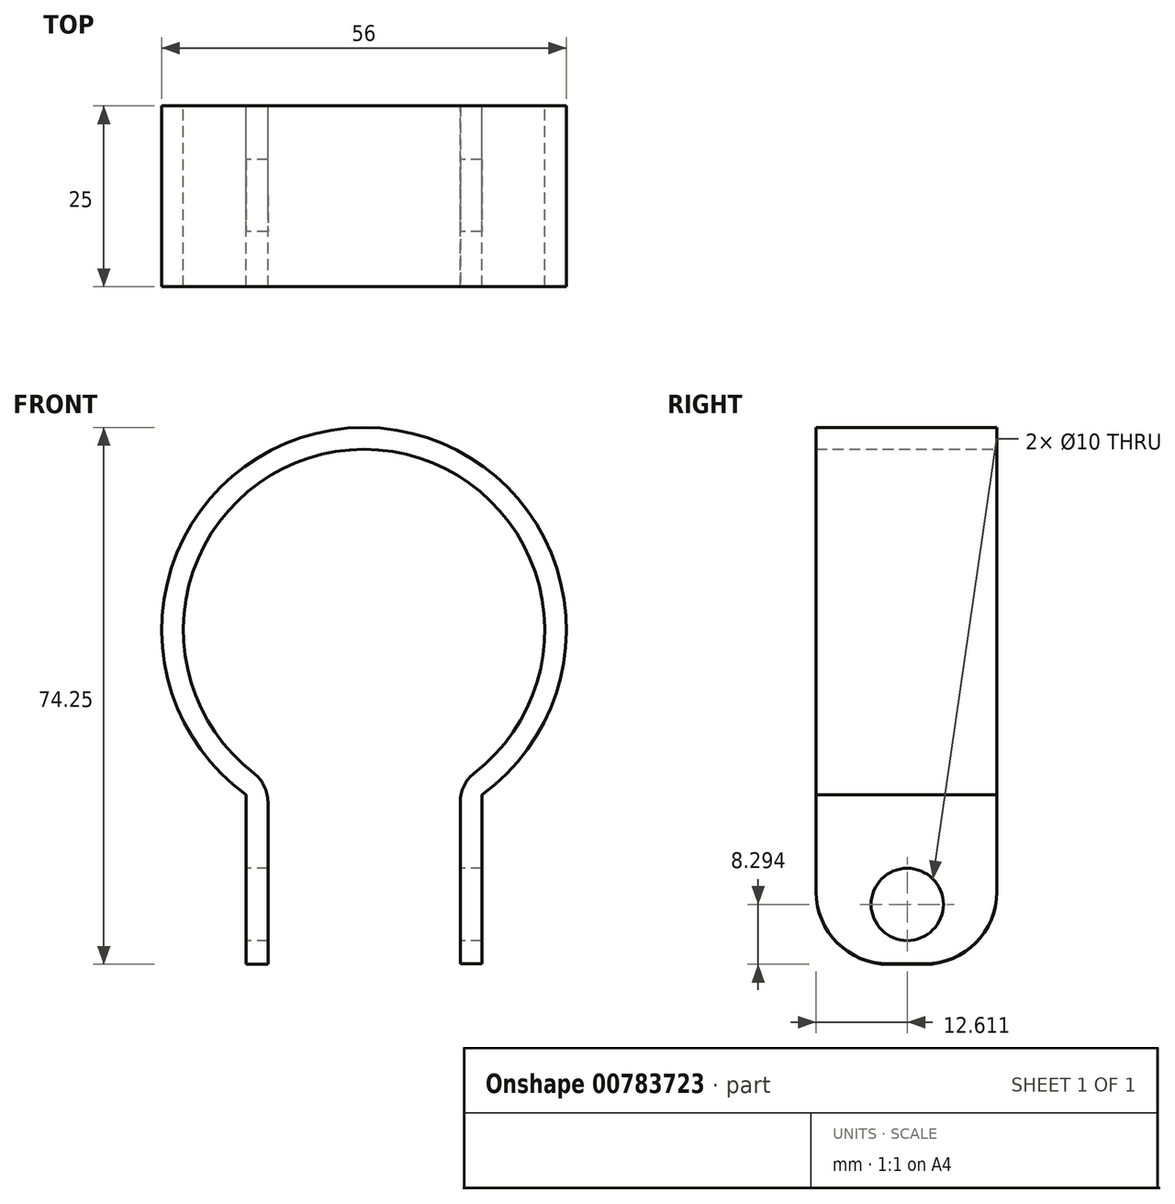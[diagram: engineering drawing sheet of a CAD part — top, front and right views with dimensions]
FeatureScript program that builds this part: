
annotation { "Feature Type Name" : "Feature", "Feature Type Description" : "" }
export const myFeature = defineFeature(function(context is Context, id is Id, definition is map)
    precondition{}
    {
        {
            var Q0;
            Q0=qCreatedBy(makeId("Front.planeOp"),FACE);
            var sketch = newSketch(context, id + "F0", { "sketchPlane" : qUnion([Q0])});
            skLineSegment(sketch, "E0", {"start": v(0, 573.91) * mm, "end": v(0, 0) * mm, "construction": true});
            skArc(sketch, "E1", {"start": v(13.3, -21.17) * mm, "mid": v(0, 25) * mm, "end": v(-13.3, -21.17) * mm});
            skLineSegment(sketch, "E2", {"start": v(-13.3, -21.17) * mm, "end": v(-13.3, -46.17) * mm});
            skLineSegment(sketch, "E3.top", {"start": v(-13.3, -46.25) * mm, "end": v(-16.3, -46.25) * mm});
            skLineSegment(sketch, "E3.left", {"start": v(-13.3, -21.17) * mm, "end": v(-13.3, -46.25) * mm});
            skLineSegment(sketch, "E3.right", {"start": v(-16.3, -22.77) * mm, "end": v(-16.3, -46.25) * mm});
            skArc(sketch, "E4.0", {"start": v(16.3, -22.77) * mm, "mid": v(0, 28) * mm, "end": v(-16.3, -22.77) * mm});
            skLineSegment(sketch, "E5.top", {"start": v(13.3, -46.17) * mm, "end": v(16.3, -46.17) * mm});
            skLineSegment(sketch, "E5.left", {"start": v(13.3, -21.17) * mm, "end": v(13.3, -46.17) * mm});
            skLineSegment(sketch, "E5.right", {"start": v(16.3, -22.77) * mm, "end": v(16.3, -46.17) * mm});
            skSolve(sketch);
        }
        {
            var Q0;
            Q0=makeQuery(id+"F0.imprint","IMPRINT",FACE,{"disambiguationData":[TD([[makeQuery(id+"F0.imprint","IMPRINT",EDGE,{"derivedFrom":sQuery(id+"F0.wireOp",EDGE,"E1")}),-1.0]])]});
            extrude(context, id + "F1", {"entities" : qUnion([Q0]), "depth" : 25 * mm, "offsetDistance" : 25 * mm});
        }
        {
            var Q0;
            Q0=makeQuery(id+"F1.opExtrude","SWEPT_EDGE",EDGE,{"disambiguationData":[OSD([sQuery(id+"F0.wireOp",EDGE,"E1"),sQuery(id+"F0.wireOp",EDGE,"fyjrehtl-utBM-2CSD-NGM8-mUDq3fJwo4ss")])]});
            var Q1;
            Q1=makeQuery(id+"F1.opExtrude","SWEPT_EDGE",EDGE,{"disambiguationData":[OSD([sQuery(id+"F0.wireOp",EDGE,"d362fed6-9a36-432e-b8db-d3779c36aab3.0"),sQuery(id+"F0.wireOp",EDGE,"678f56e4-17c6-4ce1-a282-9cf292f3273f.0")])]});
            var Q2;
            Q2=makeQuery(id+"F1.opExtrude","SWEPT_EDGE",EDGE,{"disambiguationData":[OSD([sQuery(id+"F0.wireOp",EDGE,"E1"),sQuery(id+"F0.wireOp",EDGE,"E2")])]});
            var Q3;
            Q3=makeQuery(id+"F1.opExtrude","SWEPT_EDGE",EDGE,{"disambiguationData":[OSD([sQuery(id+"F0.wireOp",EDGE,"d362fed6-9a36-432e-b8db-d3779c36aab3.0"),sQuery(id+"F0.wireOp",EDGE,"6adaac5c-5b7c-4ea6-af30-f9cbe7f82b5f.0")])]});
            fillet(context, id + "F2", {"entities" : qUnion([Q0, Q1, Q2, Q3]), "radius" : 5 * mm, "tangentPropagation" : true, "allowEdgeOverflow" : false});
        }
        {
            var Q0;
            Q0=makeQuery(id+"F1.opExtrude","SWEPT_FACE",FACE,{"disambiguationData":[OSD([sQuery(id+"F0.wireOp",EDGE,"E3.right")])]});
            var sketch = newSketch(context, id + "F3", { "sketchPlane" : qUnion([Q0])});
            skCircle(sketch, "E6", {"center": v(12.39, -37.96) * mm, "radius": 5 * mm});
            skSolve(sketch);
        }
        {
            var Q0;
            Q0=makeQuery(id+"F3.imprint","IMPRINT",FACE,{"disambiguationData":[TD([[makeQuery(id+"F3.imprint","IMPRINT",EDGE,{"derivedFrom":sQuery(id+"F3.wireOp",EDGE,"E6")}),1.0]])]});
            extrude(context, id + "F4", {"entities" : qUnion([Q0]), "operationType" : NewBodyOperationType.REMOVE, "oppositeDirection" : true, "depth" : 42.9 * mm, "offsetDistance" : 25 * mm});
        }
        {
            var Q0;
            Q0=makeQuery(id+"F1.opExtrude","CAP_EDGE",EDGE,{"disambiguationData":[OSD([sQuery(id+"F0.wireOp",EDGE,"E3.top")])],"isStart":true});
            var Q1;
            Q1=makeQuery(id+"F1.opExtrude","CAP_EDGE",EDGE,{"disambiguationData":[OSD([sQuery(id+"F0.wireOp",EDGE,"E3.top")])],"isStart":false});
            var Q2;
            Q2=makeQuery(id+"F1.opExtrude","CAP_EDGE",EDGE,{"disambiguationData":[OSD([sQuery(id+"F0.wireOp",EDGE,"E5.top")])],"isStart":false});
            var Q3;
            Q3=makeQuery(id+"F1.opExtrude","CAP_EDGE",EDGE,{"disambiguationData":[OSD([sQuery(id+"F0.wireOp",EDGE,"E5.top")])],"isStart":true});
            fillet(context, id + "F5", {"entities" : qUnion([Q0, Q1, Q2, Q3]), "radius" : 10 * mm, "tangentPropagation" : true, "allowEdgeOverflow" : false});
        }
    });
